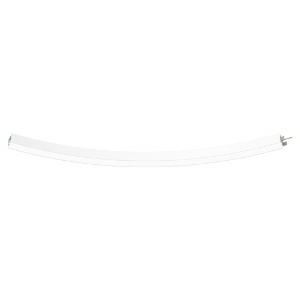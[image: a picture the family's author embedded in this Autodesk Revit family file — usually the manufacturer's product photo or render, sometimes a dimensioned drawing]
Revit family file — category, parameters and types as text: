
# Revit family: super-g_slim_super_g_slim_5200_45degdeg_hl_ps_led__42w_5530lm_3000k_cri_80_430-1740_b0aa
name_source: partatom
category: Leuchten
revit_build: Autodesk Revit 2016 (Build: 20190508_0715(x64)
units: mm (PartAtom-declared; Revit-internal decimal feet)

## family parameters
Basisbauteil = Fläche
Beim Laden mit Abzugskörper schneiden = Nein
Bemaßung runder Anschluss = Durchmesser verwenden
Gemeinsam genutzt = Nein
Lichtquelle = Nein
Raumberechnungspunkt = Nein
Teiletyp = Normal

## types (1)
- 430-1740-D01 (1 x LED, 480 lm, 3000K)
    Approval mark = CE
    Beschreibung = The insert consists of aluminum-extruded profile. Charming SOFT-EDGE design ensure unparalleled styling. The ballast is integrated and allows for an operation with 220-240V (50/60Hz). SUPER-G SLIM (# 430-1740) ist not dimmable (on/off).
    CIE Flux Codes = 48 79 96 100 71
    Color Rendering = 1B/80…89
    Color Temperature = 3000K
    Height = 90 mm
    Hersteller = Prolicht
    Lamp Light Flux = 480 lm
    Lamp count = 1
    Lampe = 1 x LED
    Length = 146 mm
    Luminous efficacy = 103 lm/W
    ModVariant = Nein
    Modell = 430-1740
    Mounting Place = Ceiling
    Mounting Type = Pendant
    Number of Poles = 1
    OnlyDefault = Ja
    Power Factor = 1
    Product Name = SUPER-G SLIM__SUPER G SLIM 5200/45°° HL PS LED: 42W 5530lm 3000K CRI:80
    Product group = Suspended profile systems
    ProductGroupID = 944
    Protection Class = Protection class I
    Protection Degree = IP 20
    RLX_Detail_Level = 1
    RlxData = <blob elided: 34965 chars, md5=f7cc532a>
    Scheinlast = 46 VA
    Socket = socket
    Standby Power = 0 W
    System Light Flux = 4765 lm
    System Power = 46 W
    Typenbild = 430-1740.jpg
    URL = http://relux.com
    VarID = 430-1740-d01
    Voltage = 0 V
    Vorgabe-Ansicht = 1800 mm
    Weight = 0.00 kg
    Width = 65 mm

## geometry (parser evidence)
native form markers: Sweep x42
no freeform markers — native parametric forms only
